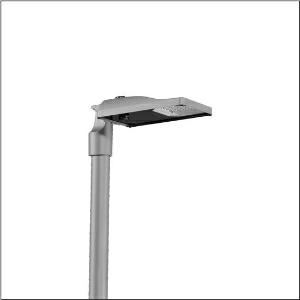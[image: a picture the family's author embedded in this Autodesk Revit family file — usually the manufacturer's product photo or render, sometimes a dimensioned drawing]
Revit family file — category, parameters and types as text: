
# Revit family: streetlight_sl_31_micro___st0_5a_5xh5b31t08ca_3c37
name_source: partatom
category: Lighting Fixtures
units: mm (PartAtom-declared; Revit-internal decimal feet)

## family parameters
Cut with Voids When Loaded = No
Host = Face
Light Source = No
Part Type = Normal
Room Calculation Point = No
Round Connector Dimension = Use Diameter
Shared = No

## types (1)
- --- (1 x LED, 1440 lm, 10.2 W, 3000K)
    Apparent Load = 10 VA
    CIE Flux Codes = 41 75 97 100 100
    Color Rendering = 70
    Color Temperature = 3000K
    Default Elevation = 1800 mm
    Description = Streetlight SL 31 micro D4i, Desk-Remote mast luminaire for post-top, side-entry; light control with lens of PMMA; light distribution: ST0.5a, direct asymmetric distribution, for standard-compliant lighting for roads and squares; LED: luminous flux: 1.440lm, light colour: 730, colour temperature: 3000K; luminous efficacy: 141,2lm/W; control: pre-setting: logarithmic dimming characteristic, flexible luminous flux parameterisation, time-dependent luminous flux control, constant luminous flux control, power reduction, intelligent temperature release in ECG and LED module, overheat protection; luminaire housing, of diecast aluminium, SITECO metallic grey (DB 702S), corrosivity category C5 high according to DIN EN ISO 12944; cover of toughened safety glass, transparent, opened without tools; mast flange of diecast aluminium, SITECO metallic grey (DB 702S), spigot size: 76/60mm, mast flange included unmounted; cable length: 5,5m, connection cable pre-assembled; mains connection: 220..240V, AC, 50/60Hz; power consumption (at start of service life): 10,2W / (at end of service life): 10,5W / (with reduced operation 50%): 5,3W; protection rating (complete): IP66; insulation class (complete): insulation class II (safety insulation); impact resistance: IK09; certification: CE, ENEC, ENEC+, VDE, UKCA, ZD4i; permissible operating ambient temperature for outdoor applications: -40..+50°C; packaging unit: 1 piece

Light Distribution: ST0.5a
    Height = 76 mm
    Lamp = 1 x LED
    Lamp Light Flux = 1440 lm
    Lamp Power = 10.2 W
    Lamp count = 1
    Length = 467 mm
    Luminous efficacy = 141 lm/W
    Manufacturer = Siteco
    ModVariant = No
    Model = 5XH5B31T08CA
    Mounting Place = Pole
    Mounting Type = Pole top
    Number of Poles = 1
    OnlyDefault = Yes
    Power Factor = 1
    Product Name = Streetlight SL 31 micro | ST0.5a
    Product group = mast luminaire | pylon top
    ProductGroupID = 6100
    Protection Class = Protection class II
    Protection Degree = IP 66
    RLX_Detail_Level = 1
    RLX_Emergency_Light_Flux = 0 lm
    RLX_Emergency_Type = 0
    RLX_Emergency_Type_DB = No
    RlxData = <blob elided: 55113 chars, md5=5e30deac>
    Socket = socket
    Standby Power = 0 W
    System Light Flux = 1440 lm
    System Power = 10 W
    Type Comments = factory setting: luminous flux: 100 % | dim-lin: 254 | 386 mA
    Type Image = l_1300315.jpg
    URL = http://relux.com
    VarID = @adj_057181
    Voltage = 0 V
    Weight = 0.00 kg
    Width = 265 mm

## geometry (parser evidence)
native form markers: Blend x4, Sweep x11
no freeform markers — native parametric forms only
